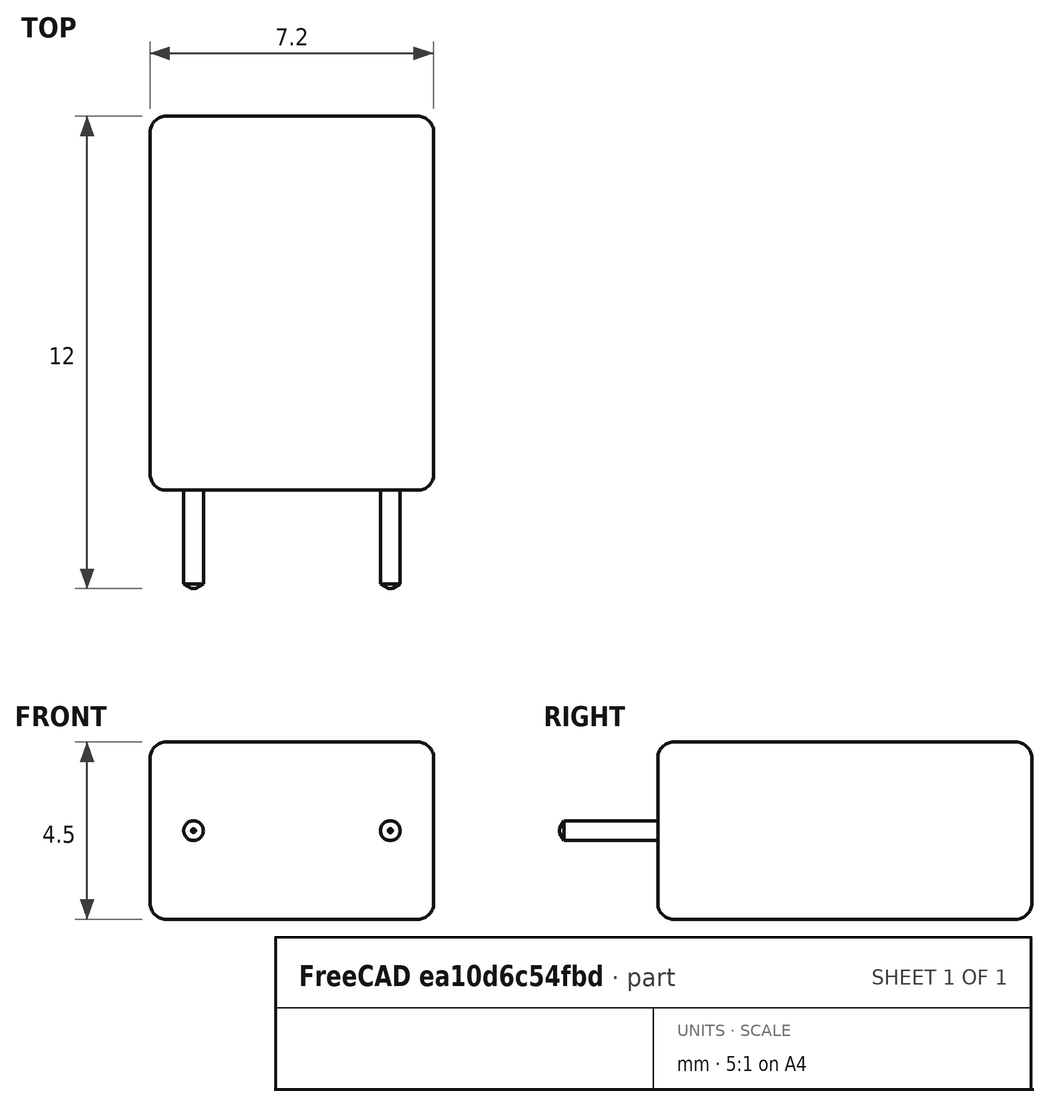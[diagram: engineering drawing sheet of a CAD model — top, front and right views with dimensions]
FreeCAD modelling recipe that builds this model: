
FCSTD DOCUMENT  (FreeCAD 0.17R13528 (Git))
Label: WIMA_E_Case
License: All rights reserved
LicenseURL: http://en.wikipedia.org/wiki/All_rights_reserved
objects: Part::Part2DObjectPython×6, Part::Feature×1
note: 7 computed .brp shape members not serialized (recipe doc carries the construction recipe); baked Part::Feature solids carry a one-line shape summary decoded from their .brp

FEATURE [Part::Part2DObjectPython] ShapeString  label="F_WIMA"  # Draft 2D object (typed FeaturePython)
  FontFile = <userpath>/Desktop/Freecad Projects/calibrib.ttf
  Placement = pos=(-0.75,3.5,2.26) rot=(0,0,1;0rad)
  Size = 1.75
  String = WIMA
  Tracking = 0
FEATURE [Part::Part2DObjectPython] ShapeString001  label="F_Vaule/Rating"  # Draft 2D object (typed FeaturePython)
  FontFile = <userpath>/Desktop/Freecad Projects/calibrib.ttf
  Placement = pos=(-0.65,2.25,2.26) rot=(0,0,1;0rad)
  Size = 1
  String = 0.100/250V
  Tracking = 0
FEATURE [Part::Part2DObjectPython] ShapeString002  label="F_Tolerance"  # Draft 2D object (typed FeaturePython)
  FontFile = <userpath>/Desktop/Freecad Projects/calibrib.ttf
  Placement = pos=(-0.65,1,2.26) rot=(0,0,1;0rad)
  Size = 1
  String = 10
  Tracking = 0
FEATURE [Part::Part2DObjectPython] ShapeString003  label="B_WIMA"  # Draft 2D object (typed FeaturePython)
  FontFile = <userpath>/Desktop/Freecad Projects/calibrib.ttf
  Placement = pos=(5,3.5,-2.26) rot=(0,1,0;3.14159rad)
  Size = 1.75
  String = WIMA
  Tracking = 0
FEATURE [Part::Part2DObjectPython] ShapeString004  label="B_Value/Tolerance"  # Draft 2D object (typed FeaturePython)
  FontFile = <userpath>/Desktop/Freecad Projects/calibrib.ttf
  Placement = pos=(4.9,2.25,-2.26) rot=(0,1,0;3.14159rad)
  Size = 1
  String = 0.100/250V
  Tracking = 0
FEATURE [Part::Part2DObjectPython] ShapeString005  label="B_Tolerance"  # Draft 2D object (typed FeaturePython)
  FontFile = <userpath>/Desktop/Freecad Projects/calibrib.ttf
  Placement = pos=(4.9,1,-2.26) rot=(0,1,0;3.14159rad)
  Size = 1
  String = 10
  Tracking = 0
FEATURE [Part::Feature] Part__Feature  label="WIMA_E_Case"
  shape: bbox 7.2 x 12 x 4.5 mm, 36 faces (baked)
